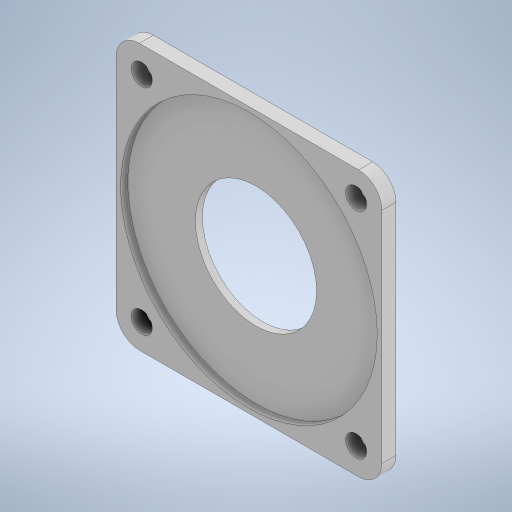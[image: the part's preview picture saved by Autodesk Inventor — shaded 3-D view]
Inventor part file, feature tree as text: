
AUTODESK INVENTOR PART (.ipt)
format: ipt  version: 2024 (Build 280153000, 153)  size: 296,448 bytes
history: native  units: in
note: dims shown in document units (in); Inventor stores cm internally (conversion verified against a paired STEP export)
features: extrude x4, sketch x4, fillet x2
ambient origin geometry x8: Origin, YZ Plane, XZ Plane, XY Plane, X Axis, Y Axis, Z Axis, Center Point
bodies: Solid1 (feature_tree)
feature tree (10):
  extrude  "Extrusion1"  Depth=4.4882in
  extrude  "Extrusion2"  Depth=0.2362in
  fillet  "Fillet1"  Radius=2.2441in
  fillet  "Fillet2"  Radius=2.2441in
  extrude  "Extrusion3"  Depth=0.3937in
  extrude  "Extrusion4"  Depth=0.3937in
  sketch  "Sketch1"  dims[d0=4.4882in d1=4.4882in]
  sketch  "Sketch2"  dims[d2=0.2362in d3=0.0in d4=4.3307in d5=2.2441in d6=2.2441in]
  sketch  "Sketch3"  dims[d7=0.1181in d8=0.0in d9=0.3937in]
  sketch  "Sketch4"  dims[d10=0.3937in d11=0.3543in d12=0.4346in d13=0.4346in d14=0.3543in d15=0.3543in d16=0.3543in d17=0.4346in d18=0.4346in d19=0.4346in d20=0.4346in d21=0.4346in d22=0.4346in d23=0.2362in d24=0.0in d25=2.0472in d26=2.2441in d27=2.2441in d28=0.3937in d29=0.0in d30=0.0197in d31=0.0344in]
